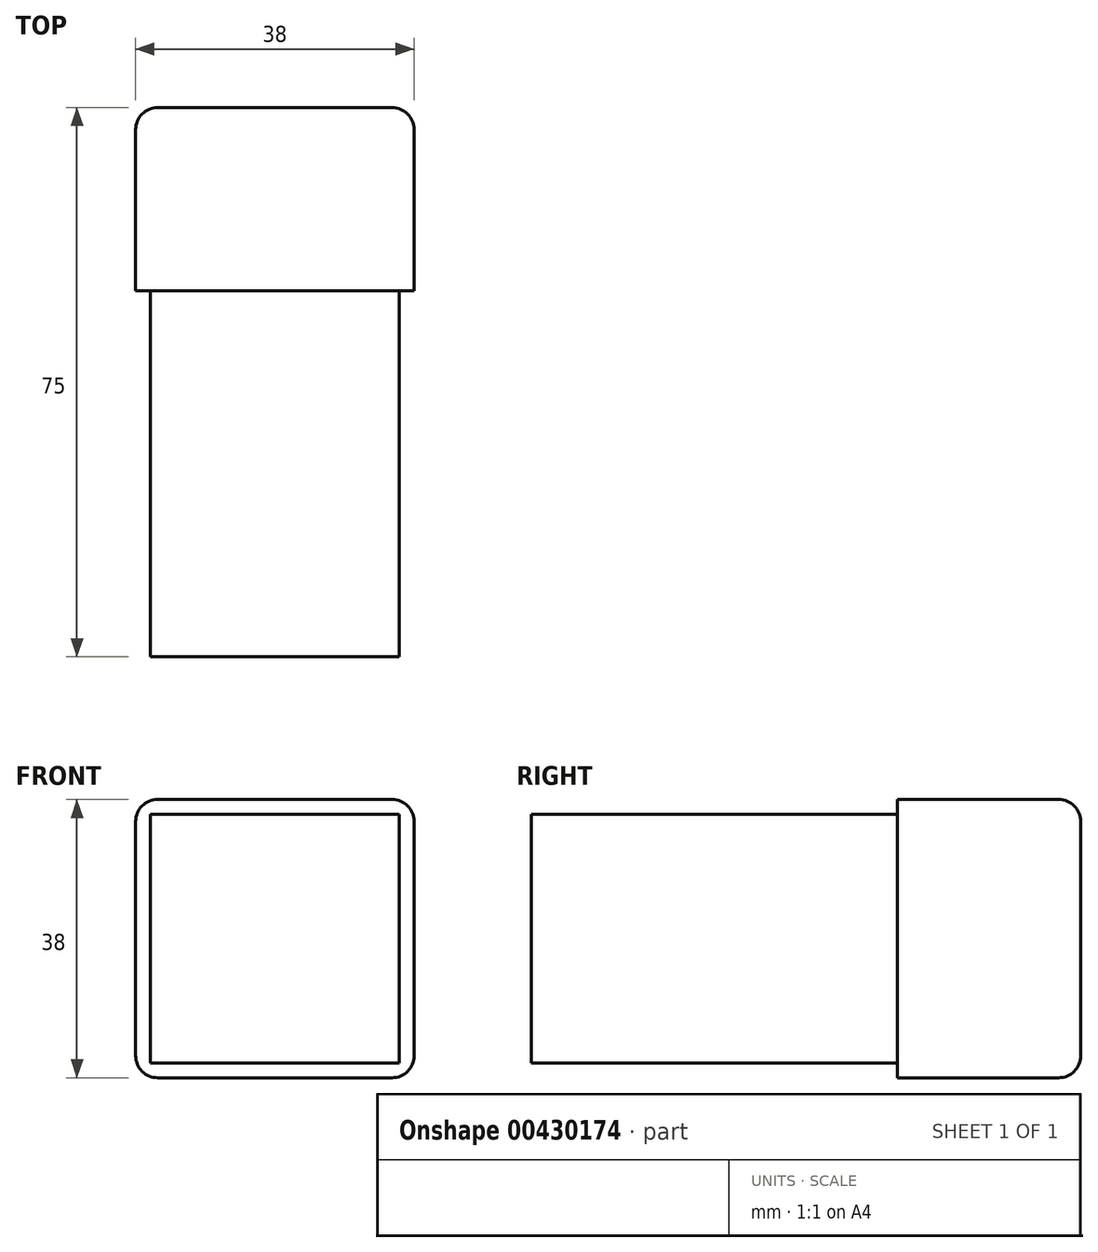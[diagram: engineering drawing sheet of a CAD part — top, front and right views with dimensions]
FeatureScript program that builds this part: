
annotation { "Feature Type Name" : "Feature", "Feature Type Description" : "" }
export const myFeature = defineFeature(function(context is Context, id is Id, definition is map)
    precondition{}
    {
        {
            var Q0;
            Q0=qCreatedBy(makeId("Front.planeOp"),FACE);
            var sketch = newSketch(context, id + "F0", { "sketchPlane" : qUnion([Q0])});
            skLineSegment(sketch, "E0.bottom", {"start": v(-18, 16.5) * mm, "end": v(16, 16.5) * mm});
            skLineSegment(sketch, "E0.top", {"start": v(-18, -17.5) * mm, "end": v(16, -17.5) * mm});
            skLineSegment(sketch, "E0.left", {"start": v(-18, 16.5) * mm, "end": v(-18, -17.5) * mm});
            skLineSegment(sketch, "E0.right", {"start": v(16, 16.5) * mm, "end": v(16, -17.5) * mm});
            skLineSegment(sketch, "E1.top", {"start": v(-20, -19.5) * mm, "end": v(18, -19.5) * mm});
            skLineSegment(sketch, "E2", {"start": v(-18, -17.5) * mm, "end": v(-1, -17.5) * mm, "construction": true});
            skLineSegment(sketch, "E3", {"start": v(18, -19.5) * mm, "end": v(18, 18.5) * mm});
            skLineSegment(sketch, "E4", {"start": v(18, 18.5) * mm, "end": v(-20, 18.5) * mm});
            skLineSegment(sketch, "E5", {"start": v(-20, 18.5) * mm, "end": v(-20, -19.5) * mm});
            skSolve(sketch);
        }
        {
            var Q0;
            Q0=makeQuery(id+"F0.imprint","IMPRINT",FACE,{"disambiguationData":[TD([[makeQuery(id+"F0.imprint","IMPRINT",EDGE,{"derivedFrom":sQuery(id+"F0.wireOp",EDGE,"E0.bottom")}),-1.0]])]});
            extrude(context, id + "F1", {"entities" : qUnion([Q0]), "depth" : 75 * mm});
        }
        {
            var Q0;
            Q0=makeQuery(id+"F0.imprint","IMPRINT",FACE,{"disambiguationData":[TD([[makeQuery(id+"F0.imprint","IMPRINT",EDGE,{"derivedFrom":sQuery(id+"F0.wireOp",EDGE,"E0.bottom")}),1.0]])]});
            extrude(context, id + "F2", {"entities" : qUnion([Q0]), "operationType" : NewBodyOperationType.ADD, "depth" : 25 * mm});
        }
        {
            var Q0;
            Q0=makeQuery(id+"F2.opExtrude","SWEPT_EDGE",EDGE,{"disambiguationData":[OSD([sQuery(id+"F0.wireOp",EDGE,"E4"),sQuery(id+"F0.wireOp",EDGE,"E5")])]});
            var Q1;
            Q1=makeQuery(id+"F2.opExtrude","SWEPT_EDGE",EDGE,{"disambiguationData":[OSD([sQuery(id+"F0.wireOp",EDGE,"E1.top"),sQuery(id+"F0.wireOp",EDGE,"E5")])]});
            var Q2;
            Q2=makeQuery(id+"F2.opExtrude","SWEPT_EDGE",EDGE,{"disambiguationData":[OSD([sQuery(id+"F0.wireOp",EDGE,"E3"),sQuery(id+"F0.wireOp",EDGE,"E4")])]});
            var Q3;
            Q3=makeQuery(id+"F2.opExtrude","CAP_EDGE",EDGE,{"disambiguationData":[OSD([sQuery(id+"F0.wireOp",EDGE,"E4")])],"isStart":true});
            var Q4;
            Q4=makeQuery(id+"F2.opExtrude","CAP_EDGE",EDGE,{"disambiguationData":[OSD([sQuery(id+"F0.wireOp",EDGE,"E3")])],"isStart":true});
            var Q5;
            Q5=makeQuery(id+"F2.opExtrude","SWEPT_EDGE",EDGE,{"disambiguationData":[OSD([sQuery(id+"F0.wireOp",EDGE,"E1.top"),sQuery(id+"F0.wireOp",EDGE,"E3")])]});
            var Q6;
            Q6=makeQuery(id+"F2.opExtrude","CAP_EDGE",EDGE,{"disambiguationData":[OSD([sQuery(id+"F0.wireOp",EDGE,"E1.top")])],"isStart":true});
            var Q7;
            Q7=makeQuery(id+"F2.opExtrude","CAP_EDGE",EDGE,{"disambiguationData":[OSD([sQuery(id+"F0.wireOp",EDGE,"E5")])],"isStart":true});
            fillet(context, id + "F3", {"entities" : qUnion([Q0, Q1, Q2, Q3, Q4, Q5, Q6, Q7]), "radius" : 3 * mm, "tangentPropagation" : true, "allowEdgeOverflow" : false});
        }
    });
